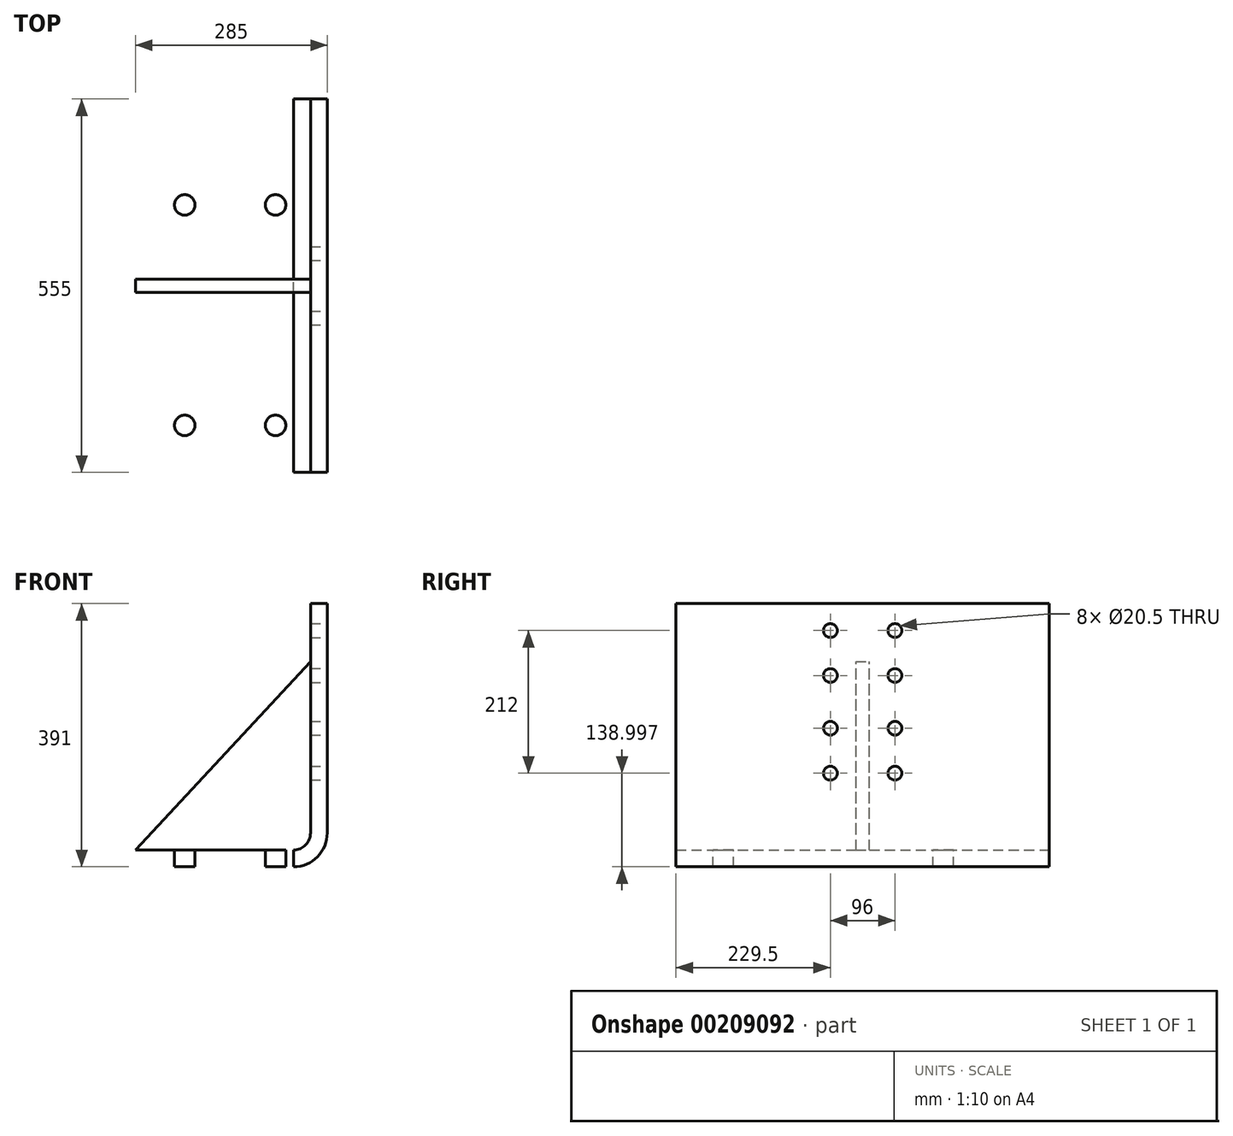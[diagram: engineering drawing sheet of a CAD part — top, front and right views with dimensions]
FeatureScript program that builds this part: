
annotation { "Feature Type Name" : "Feature", "Feature Type Description" : "" }
export const myFeature = defineFeature(function(context is Context, id is Id, definition is map)
    precondition{}
    {
        {
            var Q0;
            Q0=qCreatedBy(makeId("Front.planeOp"),FACE);
            var sketch = newSketch(context, id + "F0", { "sketchPlane" : qUnion([Q0])});
            skLineSegment(sketch, "E0", {"start": v(-219.03, -99.97) * mm, "end": v(62.97, -99.97) * mm});
            skLineSegment(sketch, "E1", {"start": v(87.97, -74.97) * mm, "end": v(87.97, 266.03) * mm});
            skLineSegment(sketch, "E2", {"start": v(87.97, 266.03) * mm, "end": v(112.97, 266.03) * mm});
            skLineSegment(sketch, "E3", {"start": v(112.97, 266.03) * mm, "end": v(112.97, -74.97) * mm});
            skLineSegment(sketch, "E4", {"start": v(62.97, -124.97) * mm, "end": v(-219.03, -124.97) * mm});
            skLineSegment(sketch, "E5", {"start": v(-219.03, -124.97) * mm, "end": v(-219.03, -99.97) * mm});
            skPoint(sketch, "E6.visualSharp", {"position": v(87.97, -99.97) * mm});
            skArc(sketch, "E6.filletArc", {"start": v(62.97, -99.97) * mm, "mid": v(80.65, -92.65) * mm, "end": v(87.97, -74.97) * mm});
            skPoint(sketch, "E7.visualSharp", {"position": v(112.97, -124.97) * mm});
            skArc(sketch, "E7.filletArc", {"start": v(62.97, -124.97) * mm, "mid": v(98.33, -110.33) * mm, "end": v(112.97, -74.97) * mm});
            skSolve(sketch);
        }
        {
            var Q0;
            Q0=qSketchRegion(id+"F0",true);
            var Q1;
            Q1=makeQuery(id+"F0.imprint","IMPRINT",FACE,{"disambiguationData":[TD([[makeQuery(id+"F0.imprint","IMPRINT",EDGE,{"derivedFrom":sQuery(id+"F0.wireOp",EDGE,"E0")}),-1.0]])]});
            extrude(context, id + "F1", {"entities" : qUnion([Q0, Q1]), "depth" : 555 * mm, "symmetric" : true});
        }
        {
            var Q0;
            Q0=makeQuery(id+"F1.opExtrude","SWEPT_FACE",FACE,{"disambiguationData":[OSD([sQuery(id+"F0.wireOp",EDGE,"E3")])]});
            var sketch = newSketch(context, id + "F2", { "sketchPlane" : qUnion([Q0])});
            skCircle(sketch, "E8", {"center": v(-48, 14.03) * mm, "radius": 10.25 * mm});
            skCircle(sketch, "E9.MirrorC", {"center": v(48, 14.03) * mm, "radius": 10.25 * mm});
            skCircle(sketch, "E10.MirrorC", {"center": v(-48, 80.83) * mm, "radius": 10.25 * mm});
            skCircle(sketch, "E11.MirrorC", {"center": v(48, 80.83) * mm, "radius": 10.25 * mm});
            skCircle(sketch, "E12.MirrorC", {"center": v(-48, 159.23) * mm, "radius": 10.25 * mm});
            skCircle(sketch, "E13.MirrorC", {"center": v(48, 159.23) * mm, "radius": 10.25 * mm});
            skCircle(sketch, "E14.MirrorC", {"center": v(-48, 226.03) * mm, "radius": 10.25 * mm});
            skCircle(sketch, "E15.MirrorC", {"center": v(48, 226.03) * mm, "radius": 10.25 * mm});
            skSolve(sketch);
        }
        {
            var Q0;
            Q0=qSketchRegion(id+"F2",true);
            extrude(context, id + "F3", {"entities" : qUnion([Q0]), "operationType" : NewBodyOperationType.REMOVE, "oppositeDirection" : true, "depth" : 25 * mm});
        }
        {
            var Q0;
            Q0=makeQuery(id+"F1.opExtrude","SWEPT_FACE",FACE,{"disambiguationData":[OSD([sQuery(id+"F0.wireOp",EDGE,"E0")])]});
            var sketch = newSketch(context, id + "F4", { "sketchPlane" : qUnion([Q0])});
            skCircle(sketch, "E16", {"center": v(35.97, -120) * mm, "radius": 15.25 * mm});
            skCircle(sketch, "E17", {"center": v(-99.03, -120) * mm, "radius": 15.25 * mm});
            skCircle(sketch, "E18.MirrorC", {"center": v(35.97, 120) * mm, "radius": 15.25 * mm});
            skCircle(sketch, "E19.MirrorC", {"center": v(-99.03, 120) * mm, "radius": 15.25 * mm});
            skCircle(sketch, "E20", {"center": v(-99.03, 207.5) * mm, "radius": 15.25 * mm});
            skCircle(sketch, "E21", {"center": v(35.97, 207.5) * mm, "radius": 15.25 * mm});
            skCircle(sketch, "E22.MirrorC", {"center": v(-99.03, -207.5) * mm, "radius": 15.25 * mm});
            skCircle(sketch, "E23.MirrorC", {"center": v(35.97, -207.5) * mm, "radius": 15.25 * mm});
            skSolve(sketch);
        }
        {
            var Q0;
            Q0=makeQuery(id+"F4.imprint","IMPRINT",FACE,{"disambiguationData":[TD([[makeQuery(id+"F4.imprint","IMPRINT",EDGE,{"derivedFrom":sQuery(id+"F4.wireOp",EDGE,"E17")}),1.0]])]});
            var Q1;
            Q1=makeQuery(id+"F4.imprint","IMPRINT",FACE,{"disambiguationData":[TD([[makeQuery(id+"F4.imprint","IMPRINT",EDGE,{"derivedFrom":sQuery(id+"F4.wireOp",EDGE,"E16")}),1.0]])]});
            var Q2;
            Q2=makeQuery(id+"F4.imprint","IMPRINT",FACE,{"disambiguationData":[TD([[makeQuery(id+"F4.imprint","IMPRINT",EDGE,{"derivedFrom":sQuery(id+"F4.wireOp",EDGE,"E19.MirrorC")}),-1.0]])]});
            var Q3;
            Q3=makeQuery(id+"F4.imprint","IMPRINT",FACE,{"disambiguationData":[TD([[makeQuery(id+"F4.imprint","IMPRINT",EDGE,{"derivedFrom":sQuery(id+"F4.wireOp",EDGE,"E18.MirrorC")}),-1.0]])]});
            var Q4;
            Q4=makeQuery(id+"F4.imprint","IMPRINT",FACE,{"disambiguationData":[TD([[makeQuery(id+"F4.imprint","IMPRINT",EDGE,{"derivedFrom":sQuery(id+"F4.wireOp",EDGE,"E20")}),1.0]])]});
            var Q5;
            Q5=makeQuery(id+"F4.imprint","IMPRINT",FACE,{"disambiguationData":[TD([[makeQuery(id+"F4.imprint","IMPRINT",EDGE,{"derivedFrom":sQuery(id+"F4.wireOp",EDGE,"E21")}),1.0]])]});
            var Q6;
            Q6=makeQuery(id+"F4.imprint","IMPRINT",FACE,{"disambiguationData":[TD([[makeQuery(id+"F4.imprint","IMPRINT",EDGE,{"derivedFrom":sQuery(id+"F4.wireOp",EDGE,"E22.MirrorC")}),-1.0]])]});
            var Q7;
            Q7=makeQuery(id+"F4.imprint","IMPRINT",FACE,{"disambiguationData":[TD([[makeQuery(id+"F4.imprint","IMPRINT",EDGE,{"derivedFrom":sQuery(id+"F4.wireOp",EDGE,"E23.MirrorC")}),-1.0]])]});
            extrude(context, id + "F5", {"entities" : qUnion([Q0, Q1, Q2, Q3, Q4, Q5, Q6, Q7]), "operationType" : NewBodyOperationType.REMOVE, "oppositeDirection" : true, "depth" : 25 * mm});
        }
        {
            var Q0;
            Q0=qCreatedBy(makeId("Front.planeOp"),FACE);
            var sketch = newSketch(context, id + "F6", { "sketchPlane" : qUnion([Q0])});
            skLineSegment(sketch, "E24", {"start": v(-172.03, -99.97) * mm, "end": v(87.97, 180.03) * mm});
            skLineSegment(sketch, "E25", {"start": v(-172.03, -99.97) * mm, "end": v(87.97, -99.97) * mm});
            skLineSegment(sketch, "E26", {"start": v(87.97, -99.97) * mm, "end": v(87.97, 180.03) * mm});
            skSolve(sketch);
        }
        {
            var Q0;
            Q0=makeQuery(id+"F6.imprint","IMPRINT",FACE,{"disambiguationData":[TD([[makeQuery(id+"F6.imprint","IMPRINT",EDGE,{"derivedFrom":sQuery(id+"F6.wireOp",EDGE,"E24")}),-1.0]])]});
            extrude(context, id + "F7", {"entities" : qUnion([Q0]), "operationType" : NewBodyOperationType.ADD, "depth" : 20 * mm, "symmetric" : true});
        }
    });
